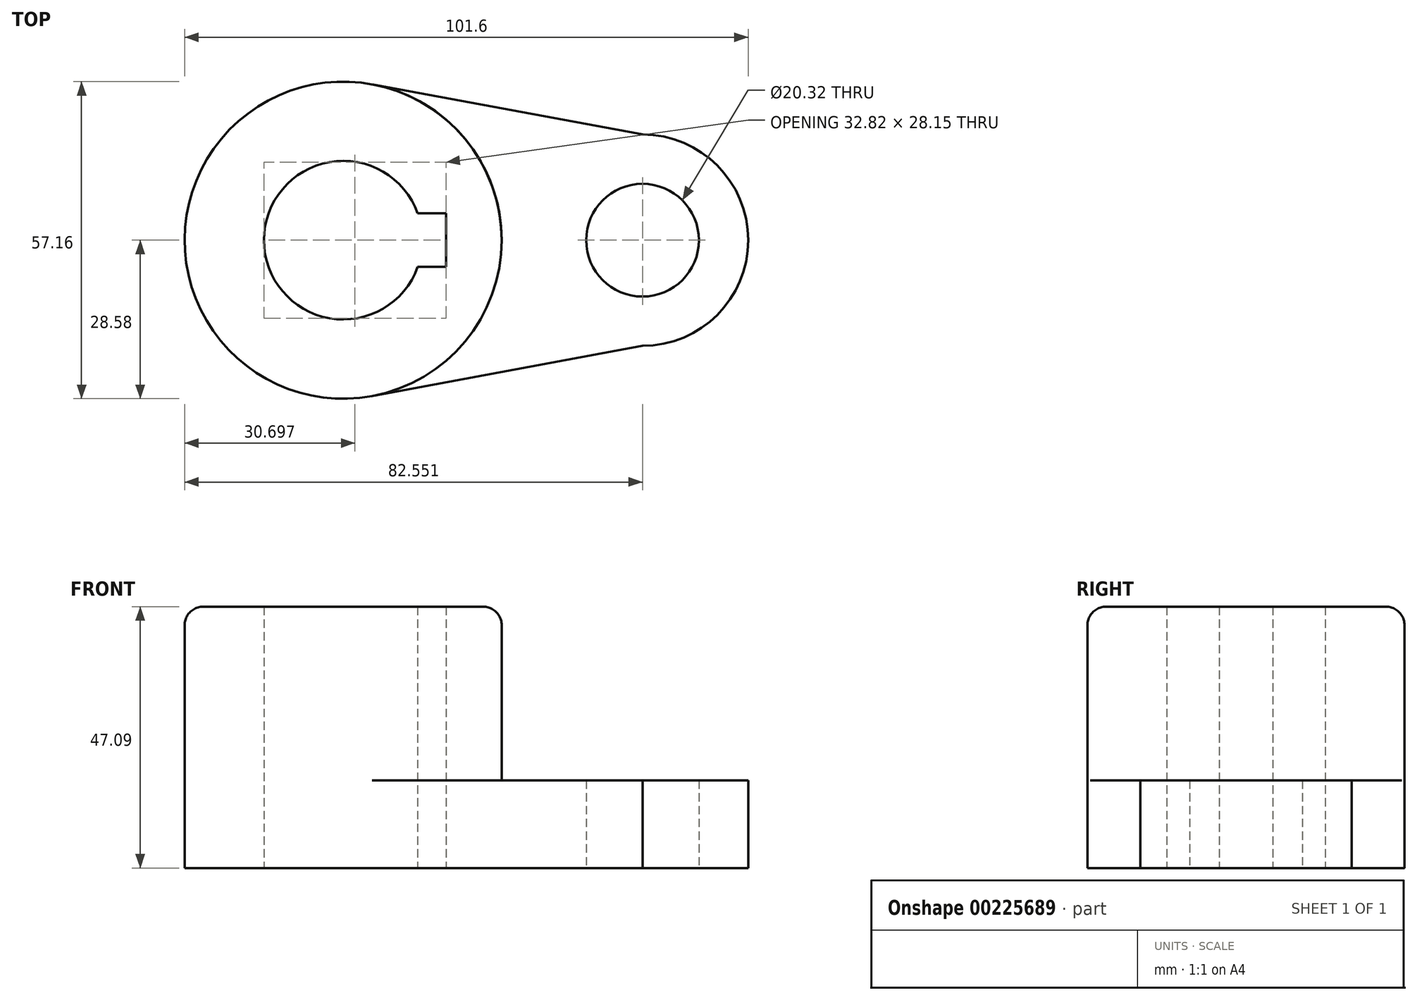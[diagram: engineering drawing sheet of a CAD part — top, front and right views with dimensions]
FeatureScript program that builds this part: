
annotation { "Feature Type Name" : "Feature", "Feature Type Description" : "" }
export const myFeature = defineFeature(function(context is Context, id is Id, definition is map)
    precondition{}
    {
        {
            var Q0;
            Q0=qCreatedBy(makeId("Top.planeOp"),FACE);
            var sketch = newSketch(context, id + "F0", { "sketchPlane" : qUnion([Q0])});
            skCircle(sketch, "E0", {"center": v(0.64, 0) * mm, "radius": 28.57 * mm});
            skCircle(sketch, "E1", {"center": v(0.64, 0) * mm, "radius": 14.29 * mm});
            skLineSegment(sketch, "E2.bottom", {"start": v(19.17, -4.83) * mm, "end": v(-19.17, -4.83) * mm});
            skLineSegment(sketch, "E2.top", {"start": v(19.17, 4.83) * mm, "end": v(-19.17, 4.83) * mm});
            skLineSegment(sketch, "E2.left", {"start": v(19.17, -4.83) * mm, "end": v(19.17, 4.83) * mm});
            skLineSegment(sketch, "E2.right", {"start": v(-19.17, -4.83) * mm, "end": v(-19.17, 4.83) * mm});
            skPoint(sketch, "E2.middle", {"position": v(0, 0) * mm});
            skCircle(sketch, "E3", {"center": v(54.61, 0) * mm, "radius": 10.16 * mm});
            skArc(sketch, "E4", {"start": v(73.66, 0) * mm, "mid": v(68.08, -13.47) * mm, "end": v(54.61, -19.05) * mm});
            skArc(sketch, "E5", {"start": v(73.66, 0) * mm, "mid": v(68.08, 13.47) * mm, "end": v(54.61, 19.05) * mm});
            skLineSegment(sketch, "E6", {"start": v(54.61, -19.05) * mm, "end": v(0, -29.18) * mm});
            skLineSegment(sketch, "E7", {"start": v(54.61, 19.05) * mm, "end": v(0, 29.18) * mm});
            skSolve(sketch);
        }
        {
            var Q0;
            {var subQ0=sQuery(id+"F0.wireOp",EDGE,"E2.left");Q0=makeQuery(id+"F0.imprint","IMPRINT",FACE,{"disambiguationData":[TD([[makeQuery(id+"F0.imprint","IMPRINT",EDGE,{"derivedFrom":subQ0}),-1.0]])]});}
            var Q1;
            {var subQ5=sQuery(id+"F0.wireOp",EDGE,"E2.right");Q1=makeQuery(id+"F0.imprint","IMPRINT",FACE,{"disambiguationData":[TD([[makeQuery(id+"F0.imprint","IMPRINT",EDGE,{"derivedFrom":subQ5}),-1.0]])]});}
            extrude(context, id + "F1", {"entities" : qUnion([Q0, Q1]), "depth" : 47.1 * mm});
        }
        {
            var Q0;
            Q0=makeQuery(id+"F0.imprint","IMPRINT",FACE,{"disambiguationData":[TD([[makeQuery(id+"F0.imprint","IMPRINT",EDGE,{"derivedFrom":sQuery(id+"F0.wireOp",EDGE,"E3")}),-1.0]])]});
            extrude(context, id + "F2", {"entities" : qUnion([Q0]), "operationType" : NewBodyOperationType.ADD, "depth" : 15.77 * mm});
        }
        {
            var Q0;
            Q0=makeQuery(id+"F1.opExtrude","CAP_EDGE",EDGE,{"disambiguationData":[OSD([sQuery(id+"F0.wireOp",EDGE,"E0")])],"isStart":false});
            fillet(context, id + "F3", {"entities" : qUnion([Q0]), "radius" : 3.3 * mm, "tangentPropagation" : true, "allowEdgeOverflow" : false});
        }
    });
